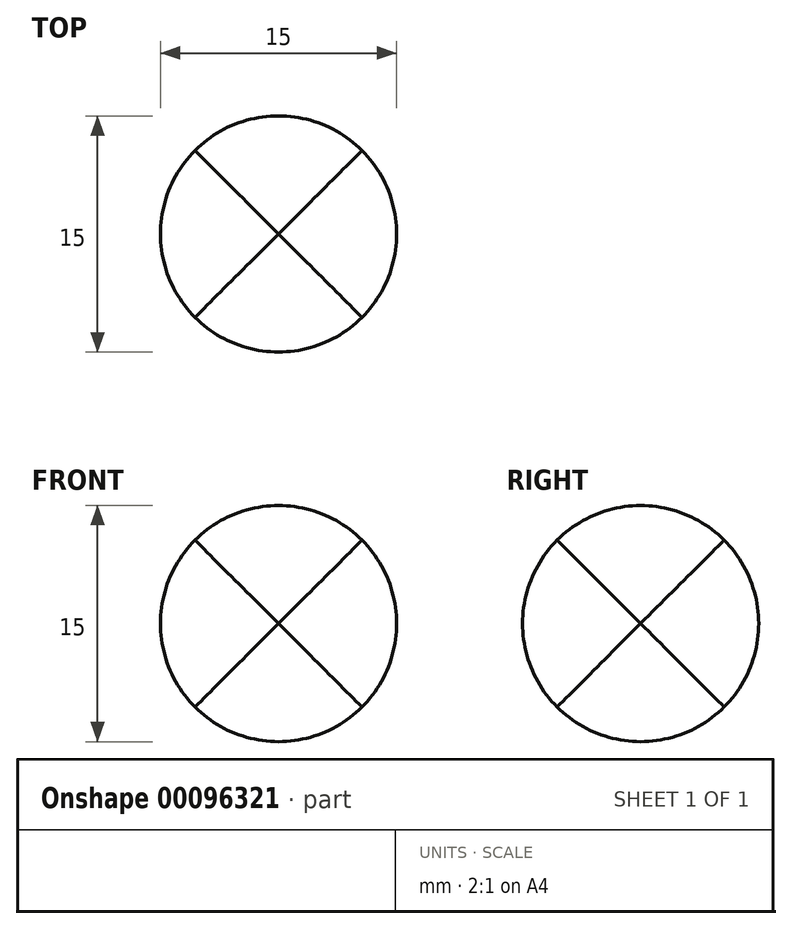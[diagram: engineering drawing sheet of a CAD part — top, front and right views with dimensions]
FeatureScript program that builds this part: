
annotation { "Feature Type Name" : "Feature", "Feature Type Description" : "" }
export const myFeature = defineFeature(function(context is Context, id is Id, definition is map)
    precondition{}
    {
        {
            var Q0;
            Q0=qCreatedBy(makeId("Front.planeOp"),FACE);
            var sketch = newSketch(context, id + "F0", { "sketchPlane" : qUnion([Q0])});
            skCircle(sketch, "E0", {"center": v(0, 0) * mm, "radius": 7.5 * mm});
            skSolve(sketch);
        }
        {
            var Q0;
            Q0=qCreatedBy(makeId("Top.planeOp"),FACE);
            var sketch = newSketch(context, id + "F1", { "sketchPlane" : qUnion([Q0])});
            skCircle(sketch, "E1", {"center": v(0, 0) * mm, "radius": 7.5 * mm});
            skSolve(sketch);
        }
        {
            var Q0;
            Q0=qCreatedBy(makeId("Right.planeOp"),FACE);
            var sketch = newSketch(context, id + "F2", { "sketchPlane" : qUnion([Q0])});
            skCircle(sketch, "E2", {"center": v(0, 0) * mm, "radius": 7.5 * mm});
            skSolve(sketch);
        }
        {
            var Q0;
            Q0 = qSketchRegion(id + "F0", true);
            extrude(context, id + "F3", {"entities" : qUnion([Q0]), "endBound" : BoundingType.SYMMETRIC, "depth" : 15 * mm});
        }
        {
            var Q0;
            Q0 = qSketchRegion(id + "F1", true);
            extrude(context, id + "F4", {"entities" : qUnion([Q0]), "operationType" : NewBodyOperationType.INTERSECT, "endBound" : BoundingType.SYMMETRIC, "depth" : 15 * mm});
        }
        {
            var Q0;
            Q0 = qSketchRegion(id + "F2", true);
            extrude(context, id + "F5", {"entities" : qUnion([Q0]), "operationType" : NewBodyOperationType.INTERSECT, "endBound" : BoundingType.SYMMETRIC, "depth" : 15 * mm});
        }
    });
